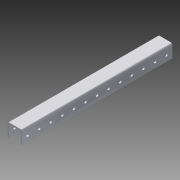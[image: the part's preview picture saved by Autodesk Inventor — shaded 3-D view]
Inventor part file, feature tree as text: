
AUTODESK INVENTOR PART (.ipt)
format: ipt  version: 2015 (Build 190159000, 159)  size: 412,160 bytes
history: native  units: in
note: dims shown in document units (in); Inventor stores cm internally (conversion verified against a paired STEP export)
features: extrude x2, sketch x2, pattern_linear x1
ambient origin geometry x8: Origin, YZ Plane, XZ Plane, XY Plane, X Axis, Y Axis, Z Axis, Center Point
bodies: Solid1 (feature_tree)
feature tree (5):
  extrude  "Extrusion1"  Depth=13.0in
  extrude  "Extrusion4"  Depth=0.5in
  pattern_linear  "Rectangular Pattern3"  Spacing1=0.0in  [1 undecoded]
  sketch  "Sketch1"  dims[d0=1.13in d1=1.25in d2=0.125in d3=0.125in d4=0.125in d5=13.0in]
  sketch  "Sketch4"  dims[d6=0.0in d34=0.5in d35=0.0in d36=0.25in d37=1.0in d38=0.0in d39=11.811in d41=1.0in d42=11.811in d44=1.0in]
note: 1 required parameter value undecoded (feature->parameter linkage not recoverable at this tier; creation-order binding heuristic only, values carry confidence <= 0.55)
